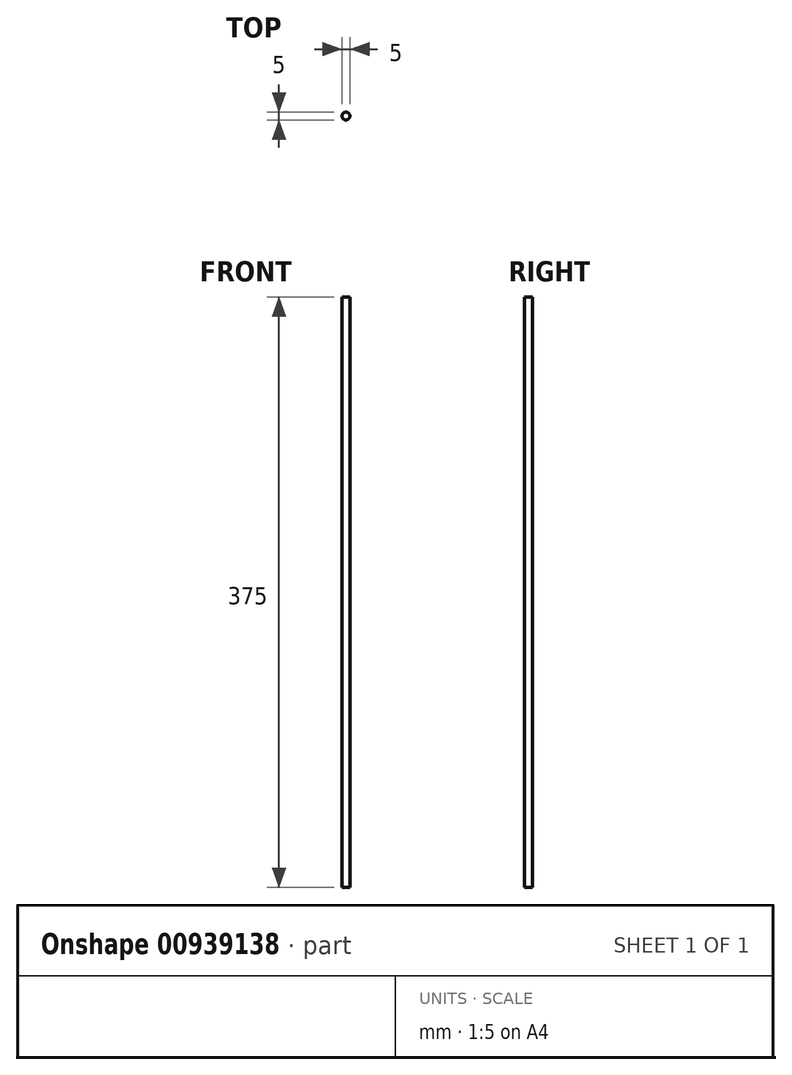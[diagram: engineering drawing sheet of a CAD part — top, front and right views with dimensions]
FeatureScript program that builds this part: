
annotation { "Feature Type Name" : "Feature", "Feature Type Description" : "" }
export const myFeature = defineFeature(function(context is Context, id is Id, definition is map)
    precondition{}
    {
        {
            var Q0;
            Q0=qCreatedBy(makeId("Top.planeOp"),FACE);
            var sketch = newSketch(context, id + "F0", { "sketchPlane" : qUnion([Q0]) });
            skCircle(sketch, "E0", {"center": v(0, 0) * mm, "radius": 2.5 * mm});
            skSolve(sketch);
        }
        {
            var Q0;
            Q0 = qSketchRegion(id + "F0", true);
            extrude(context, id + "F1", {"entities" : qUnion([Q0]), "depth" : 375 * mm, "offsetDistance" : 25 * mm});
        }
    });
